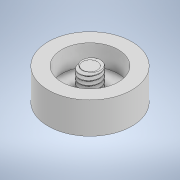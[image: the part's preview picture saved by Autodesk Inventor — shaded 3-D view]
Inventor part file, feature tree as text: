
AUTODESK INVENTOR PART (.ipt)
format: ipt  version: 2020 (Build 240168000, 168)  size: 668,160 bytes
history: native  units: in
note: dims shown in document units (in); Inventor stores cm internally (conversion verified against a paired STEP export)
features: sketch x6, extrude x3, revolve x2, thread x1, helix x1
ambient origin geometry x8: Origin, YZ Plane, XZ Plane, XY Plane, X Axis, Y Axis, Z Axis, Center Point
bodies: Solid1 (feature_tree), Solid2 (feature_tree)
feature tree (13):
  extrude  "Extrusion1"  Depth=0.375in TaperAngle=0.0deg
  extrude  "Extrusion2"  Depth=0.25in TaperAngle=0.0deg
  extrude  "Extrusion3"  Depth=0.25in TaperAngle=0.0deg
  thread  "Thread1"  [1 undecoded]
  revolve  "Revolution1"  [1 undecoded]
  revolve  "Revolution2"  [1 undecoded]
  helix  "Coil1"  [1 undecoded]
  sketch  "Sketch1"  dims[d0=1.0in d1=0.375in d2=0.0in]
  sketch  "Sketch2"  dims[d3=0.675in d4=0.25in d5=0.0in]
  sketch  "Sketch3"  dims[d6=0.25in d7=0.25in d8=0.0in d9=0.5in d10=0.0in]
  sketch  "Sketch4"  dims[d11=0.3779in d12=0.008in d13=0.008in d16=0.05in]
  sketch  "Sketch5"  dims[d18=0.3779in d20=0.0in d21=0.0in]
  sketch  "Sketch6"  dims[d22=0.05in d23=0.6in d24=0.3937in d25=0.0in d26=0.0in d27=0.0in d28=0.0in d29=0.0in]
note: 4 required parameter values undecoded (feature->parameter linkage not recoverable at this tier; creation-order binding heuristic only, values carry confidence <= 0.55)